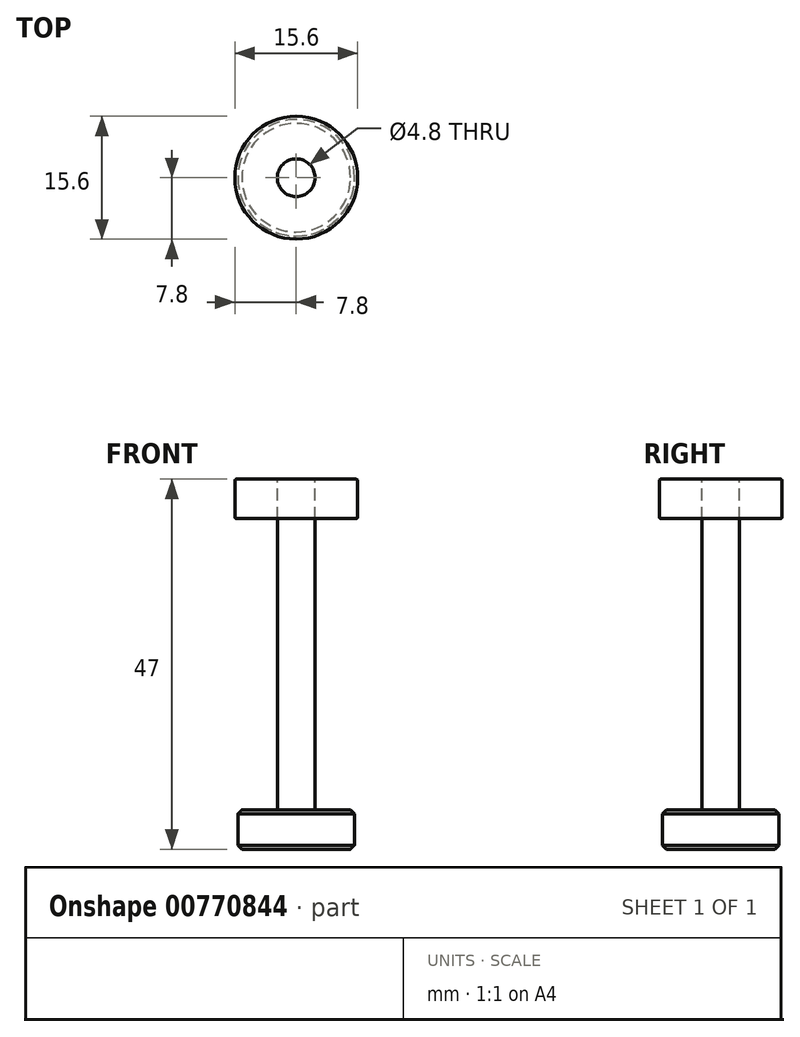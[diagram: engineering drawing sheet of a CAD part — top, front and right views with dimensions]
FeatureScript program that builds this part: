
annotation { "Feature Type Name" : "Feature", "Feature Type Description" : "" }
export const myFeature = defineFeature(function(context is Context, id is Id, definition is map)
    precondition{}
    {
        {
            var Q0;
            Q0=qCreatedBy(makeId("Front.planeOp"),FACE);
            var sketch = newSketch(context, id + "F0", { "sketchPlane" : qUnion([Q0])});
            skLineSegment(sketch, "E0", {"start": v(0, 0) * mm, "end": v(-7.4, 0) * mm});
            skLineSegment(sketch, "E1", {"start": v(-7.4, 0) * mm, "end": v(-7.4, 5) * mm});
            skLineSegment(sketch, "E2", {"start": v(-7.4, 5) * mm, "end": v(-2.4, 5) * mm});
            skLineSegment(sketch, "E3", {"start": v(-2.4, 5) * mm, "end": v(-2.4, 47) * mm});
            skLineSegment(sketch, "E4", {"start": v(-2.4, 47) * mm, "end": v(0, 47) * mm});
            skLineSegment(sketch, "E5", {"start": v(0, 47) * mm, "end": v(0, 0) * mm});
            skLineSegment(sketch, "E6.bottom", {"start": v(-2.4, 47) * mm, "end": v(-7.8, 47) * mm});
            skLineSegment(sketch, "E6.top", {"start": v(-2.4, 42) * mm, "end": v(-7.8, 42) * mm});
            skLineSegment(sketch, "E6.left", {"start": v(-2.4, 47) * mm, "end": v(-2.4, 42) * mm});
            skLineSegment(sketch, "E6.right", {"start": v(-7.8, 47) * mm, "end": v(-7.8, 42) * mm});
            skSolve(sketch);
        }
        {
            var Q0;
            Q0=makeQuery(id+"F0.imprint","IMPRINT",FACE,{"disambiguationData":[TD([[makeQuery(id+"F0.imprint","IMPRINT",EDGE,{"derivedFrom":sQuery(id+"F0.wireOp",EDGE,"E0")}),-1.0]])]});
            var Q1;
            Q1=sQuery(id+"F0.wireOp",EDGE,"E5");
            revolve(context, id + "F1", {"surfaceOperationType" : NewSurfaceOperationType.NEW, "entities" : qUnion([Q0]), "axis" : qUnion([Q1]), "revolveType" : RevolveType.FULL});
        }
        {
            var Q0;
            Q0=makeQuery(id+"F1.opRevolve","SWEPT_EDGE",EDGE,{"disambiguationData":[OSD([sQuery(id+"F0.wireOp",EDGE,"E1"),sQuery(id+"F0.wireOp",EDGE,"E2")])]});
            var Q1;
            Q1=makeQuery(id+"F1.opRevolve","SWEPT_EDGE",EDGE,{"disambiguationData":[OSD([sQuery(id+"F0.wireOp",EDGE,"E0"),sQuery(id+"F0.wireOp",EDGE,"E1")])]});
            chamfer(context, id + "F2", {"entities" : qUnion([Q0, Q1]), "width" : 0.5 * mm, "tangentPropagation" : true});
        }
        {
            var Q0;
            Q0=makeQuery(id+"F0.imprint","IMPRINT",FACE,{"disambiguationData":[TD([[makeQuery(id+"F0.imprint","IMPRINT",EDGE,{"derivedFrom":sQuery(id+"F0.wireOp",EDGE,"E6.bottom")}),1.0]])]});
            var Q1;
            Q1=sQuery(id+"F0.wireOp",EDGE,"E5");
            revolve(context, id + "F3", {"surfaceOperationType" : NewSurfaceOperationType.NEW, "entities" : qUnion([Q0]), "axis" : qUnion([Q1]), "revolveType" : RevolveType.FULL});
        }
        {
            var Q0;
            Q0=makeQuery(id+"F3.opRevolve","SWEPT_EDGE",EDGE,{"disambiguationData":[OSD([sQuery(id+"F0.wireOp",EDGE,"E6.bottom"),sQuery(id+"F0.wireOp",EDGE,"E6.right")])]});
            var Q1;
            Q1=makeQuery(id+"F3.opRevolve","SWEPT_EDGE",EDGE,{"disambiguationData":[OSD([sQuery(id+"F0.wireOp",EDGE,"E6.top"),sQuery(id+"F0.wireOp",EDGE,"E6.right")])]});
            fillet(context, id + "F4", {"entities" : qUnion([Q0, Q1]), "radius" : 0.2 * mm, "tangentPropagation" : true, "allowEdgeOverflow" : false});
        }
    });
